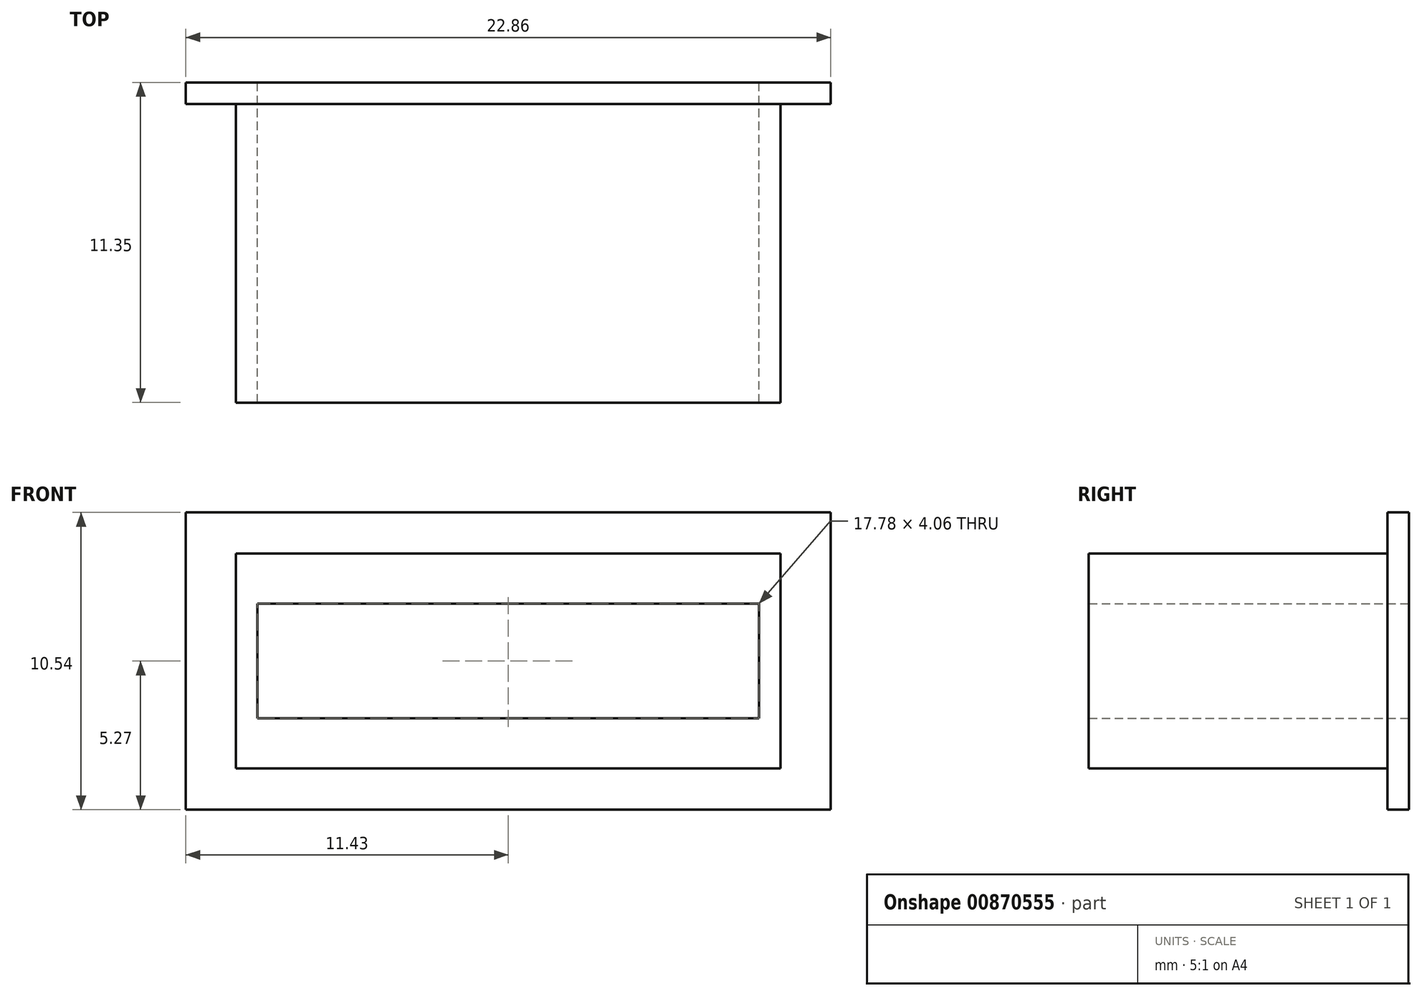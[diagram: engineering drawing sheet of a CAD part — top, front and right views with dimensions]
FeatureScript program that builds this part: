
annotation { "Feature Type Name" : "Feature", "Feature Type Description" : "" }
export const myFeature = defineFeature(function(context is Context, id is Id, definition is map)
    precondition{}
    {
        {
            var Q0;
            Q0=qCreatedBy(makeId("Front.planeOp"),FACE);
            var sketch = newSketch(context, id + "F0", { "sketchPlane" : qUnion([Q0])});
            skLineSegment(sketch, "E0.bottom", {"start": v(11.43, -5.27) * mm, "end": v(-11.43, -5.27) * mm});
            skLineSegment(sketch, "E0.top", {"start": v(11.43, 5.27) * mm, "end": v(-11.43, 5.27) * mm});
            skLineSegment(sketch, "E0.left", {"start": v(11.43, -5.27) * mm, "end": v(11.43, 5.27) * mm});
            skLineSegment(sketch, "E0.right", {"start": v(-11.43, -5.27) * mm, "end": v(-11.43, 5.27) * mm});
            skPoint(sketch, "E0.middle", {"position": v(0, 0) * mm});
            skLineSegment(sketch, "E1.bottom", {"start": v(8.9, -2.03) * mm, "end": v(-8.9, -2.03) * mm});
            skLineSegment(sketch, "E1.top", {"start": v(8.9, 2.03) * mm, "end": v(-8.9, 2.03) * mm});
            skLineSegment(sketch, "E1.left", {"start": v(8.9, -2.03) * mm, "end": v(8.9, 2.03) * mm});
            skLineSegment(sketch, "E1.right", {"start": v(-8.9, -2.03) * mm, "end": v(-8.9, 2.03) * mm});
            skSolve(sketch);
        }
        {
            var Q0;
            Q0=makeQuery(id+"F0.imprint","IMPRINT",FACE,{"disambiguationData":[TD([[makeQuery(id+"F0.imprint","IMPRINT",EDGE,{"derivedFrom":sQuery(id+"F0.wireOp",EDGE,"E0.bottom")}),-1.0]])]});
            extrude(context, id + "F1", {"entities" : qUnion([Q0]), "depth" : 0.76 * mm, "offsetDistance" : 25.4 * mm});
        }
        {
            var Q0;
            Q0=makeQuery(id+"F1.opExtrude","CAP_FACE",FACE,{"disambiguationData":[OSD([sQuery(id+"F0.wireOp",EDGE,"E0.bottom"),sQuery(id+"F0.wireOp",EDGE,"E0.top"),sQuery(id+"F0.wireOp",EDGE,"E0.left"),sQuery(id+"F0.wireOp",EDGE,"E0.right"),sQuery(id+"F0.wireOp",EDGE,"E1.bottom"),sQuery(id+"F0.wireOp",EDGE,"E1.top"),sQuery(id+"F0.wireOp",EDGE,"E1.left"),sQuery(id+"F0.wireOp",EDGE,"E1.right")])],"isStart":false});
            var sketch = newSketch(context, id + "F2", { "sketchPlane" : qUnion([Q0])});
            skLineSegment(sketch, "E2.bottom", {"start": v(8.9, -2.03) * mm, "end": v(-8.9, -2.03) * mm});
            skLineSegment(sketch, "E2.top", {"start": v(8.9, 2.03) * mm, "end": v(-8.9, 2.03) * mm});
            skLineSegment(sketch, "E2.left", {"start": v(8.9, -2.03) * mm, "end": v(8.9, 2.03) * mm});
            skLineSegment(sketch, "E2.right", {"start": v(-8.9, -2.03) * mm, "end": v(-8.9, 2.03) * mm});
            skPoint(sketch, "E2.middle", {"position": v(0, 0) * mm});
            skLineSegment(sketch, "E3.bottom", {"start": v(9.65, -3.8) * mm, "end": v(-9.65, -3.81) * mm});
            skLineSegment(sketch, "E3.top", {"start": v(9.65, 3.81) * mm, "end": v(-9.65, 3.8) * mm});
            skLineSegment(sketch, "E3.left", {"start": v(9.65, -3.8) * mm, "end": v(9.65, 3.81) * mm});
            skLineSegment(sketch, "E3.right", {"start": v(-9.65, -3.81) * mm, "end": v(-9.65, 3.81) * mm});
            skSolve(sketch);
        }
        {
            var Q0;
            Q0=makeQuery(id+"F2.imprint","IMPRINT",FACE,{"disambiguationData":[TD([[makeQuery(id+"F2.imprint","IMPRINT",EDGE,{"derivedFrom":sQuery(id+"F2.wireOp",EDGE,"E2.bottom")}),1.0]])]});
            extrude(context, id + "F3", {"entities" : qUnion([Q0]), "operationType" : NewBodyOperationType.ADD, "depth" : 10.6 * mm, "offsetDistance" : 25.4 * mm});
        }
    });
